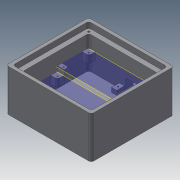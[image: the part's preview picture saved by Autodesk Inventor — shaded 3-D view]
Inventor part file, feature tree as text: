
AUTODESK INVENTOR PART (.ipt)
format: ipt  version: 2014 SP1 (Build 180222100, 222)  size: 396,800 bytes
history: native  units: in
note: dims shown in document units (in); Inventor stores cm internally (conversion verified against a paired STEP export)
features: extrude x12, sketch x12, projected_geometry x5, reference x3, fillet x2, plane x2
ambient origin geometry x8: Origin, YZ Plane, XZ Plane, XY Plane, X Axis, Y Axis, Z Axis, Center Point
bodies: Solid1 (feature_tree)
feature tree (36):
  extrude  "Extrusion1"  Depth=3.25in
  extrude  "Extrusion2"  Depth=0.1969in TaperAngle=0.0deg
  fillet  "Fillet1"  Radius=3.375in
  extrude  "Extrusion3"  Depth=0.3937in
  extrude  "Extrusion4"  Depth=1.5748in TaperAngle=0.0deg
  plane  "Work Plane1"
  extrude  "Extrusion6"  Depth=0.1875in
  fillet  "Fillet2"  Radius=0.1875in
  extrude  "Extrusion7"  Depth=0.375in
  extrude  "Extrusion8"  Depth=0.125in
  extrude  "Extrusion9"  Depth=0.1875in
  plane  "Work Plane2"
  extrude  "Extrusion10"  Depth=0.375in
  extrude  "Extrusion11"  Depth=0.75in
  extrude  "Extrusion12"  Depth=0.3937in
  extrude  "Extrusion13"  Depth=0.2362in
  sketch  "Sketch1"  dims[d0=3.375in d1=3.25in]
  sketch  "Sketch2"  dims[d2=0.3937in d3=0.1969in d4=0.0in d5=3.375in]
  sketch  "Sketch3"  dims[d6=3.25in d7=0.3937in]
  sketch  "Sketch4"  dims[d8=0.3937in d9=1.5748in d10=0.0in]
  sketch  "Sketch6"  dims[d11=0.125in d12=0.1875in d13=0.1875in]
  sketch  "Sketch7"  dims[d14=0.1875in d15=0.375in]
  sketch  "Sketch8"  dims[d16=0.375in d17=0.125in]
  reference  "Reference5"
  projected_geometry  "Projected Loop2"
  sketch  "Sketch9"  dims[d18=0.1875in d19=0.1875in]
  projected_geometry  "Projected Loop3"
  projected_geometry  "Projected Loop4"
  sketch  "Sketch10"  dims[d20=0.375in d21=0.375in]
  projected_geometry  "Projected Loop5"
  sketch  "Sketch11"  dims[d22=0.75in d23=0.75in]
  reference  "Reference7"
  reference  "Reference8"
  sketch  "Sketch12"  dims[d24=0.3937in d25=0.0in d26=0.481in]
  sketch  "Sketch13"  dims[d27=0.7559in d28=0.25in d29=0.375in d30=0.0in d31=0.25in d36=0.2756in d37=0.0in d38=0.1575in d39=0.1575in d40=0.1575in d41=0.1575in d42=0.125in d44=0.2756in d45=0.1in d46=0.5in d47=0.0in d49=0.06in d50=0.375in d51=0.0in d52=0.06in d53=0.06in d54=0.06in d55=0.5in d56=0.0in d57=0.2362in d58=0.2362in d59=0.2362in d60=0.2362in d61=0.375in d62=0.0in d63=0.06in d64=0.06in d65=0.06in d66=0.06in d67=0.06in d68=0.06in d69=0.315in d70=0.0in d71=0.2756in d72=0.1378in d73=0.2165in d74=0.1181in d75=0.0787in d76=0.0in d77=0.1181in d78=0.0591in d79=0.2362in d80=0.0in]
  projected_geometry  "Projected Loop6"
